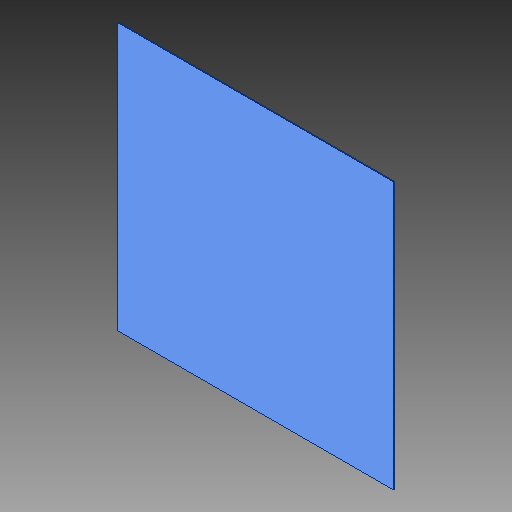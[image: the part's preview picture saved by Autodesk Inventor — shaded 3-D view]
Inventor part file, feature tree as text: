
AUTODESK INVENTOR PART (.ipt)
format: ipt  version: 2018 (Build 220112000, 112)  size: 78,848 bytes
history: native  units: in
note: dims shown in document units (in); Inventor stores cm internally (conversion verified against a paired STEP export)
features: other x1, extrude x1
ambient origin geometry x8: Origin, YZ Plane, XZ Plane, XY Plane, X Axis, Y Axis, Z Axis, Center Point
bodies: Solid1 (feature_tree)
feature tree (2):
  other  "L-NR3010, 2_2UH_81"
  extrude  "Extrusion1"  Depth=0.0004in TaperAngle=0.0deg
